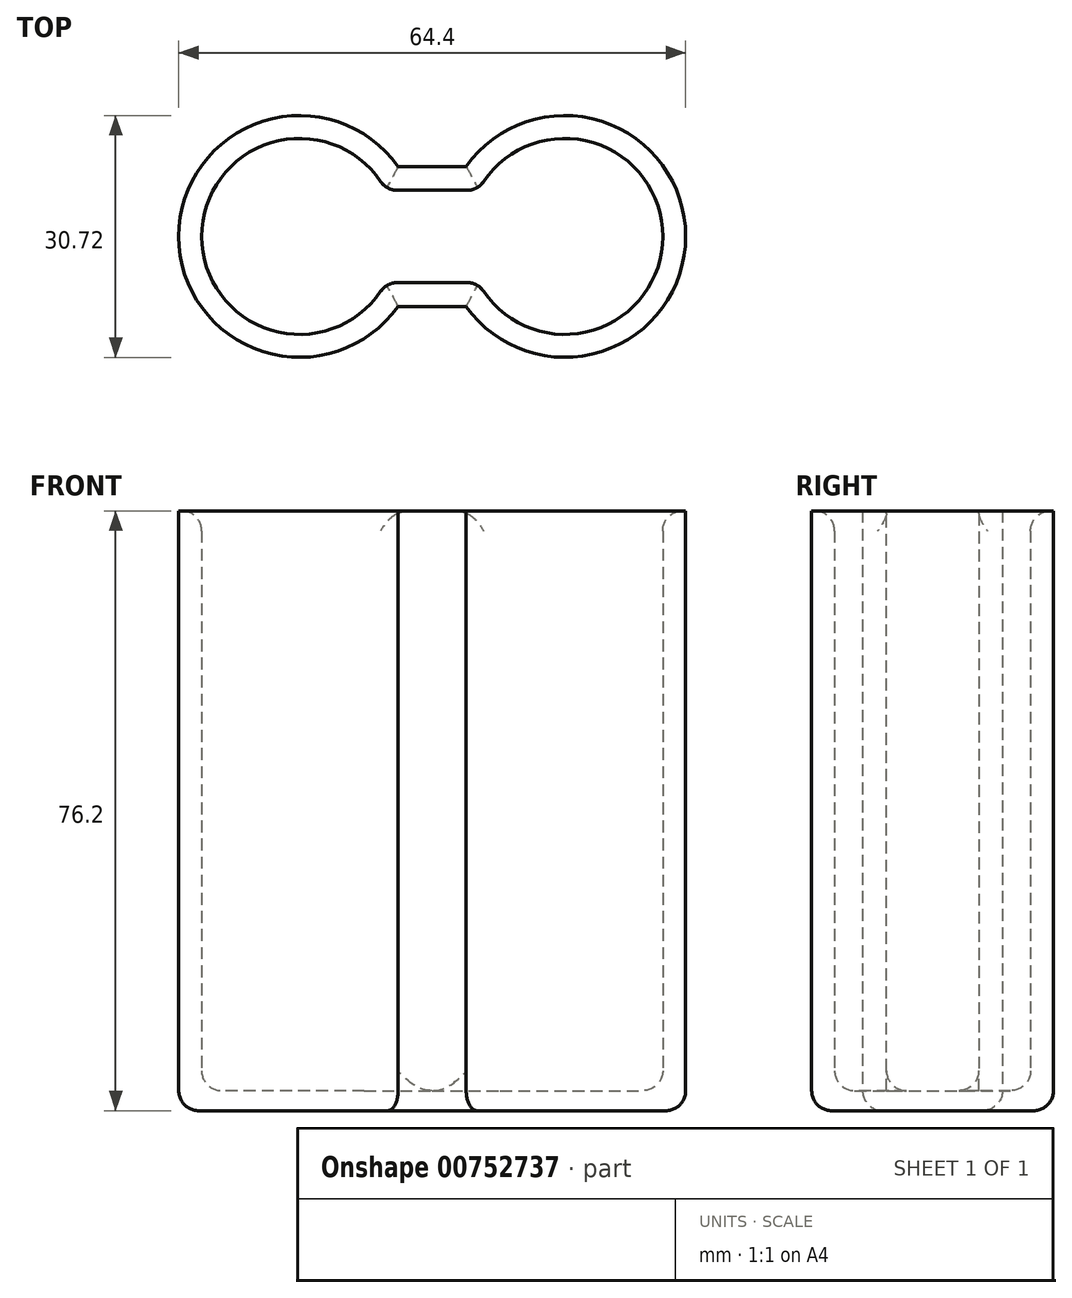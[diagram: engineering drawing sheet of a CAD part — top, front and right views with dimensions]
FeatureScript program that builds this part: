
annotation { "Feature Type Name" : "Feature", "Feature Type Description" : "" }
export const myFeature = defineFeature(function(context is Context, id is Id, definition is map)
    precondition{}
    {
        {
            var Q0;
            Q0=qCreatedBy(makeId("Top.planeOp"),FACE);
            var sketch = newSketch(context, id + "F0", { "sketchPlane" : qUnion([Q0])});
            skLineSegment(sketch, "E0.bottom", {"start": v(5.86, 5.86) * mm, "end": v(-5.86, 5.86) * mm});
            skLineSegment(sketch, "E0.top", {"start": v(5.86, -5.86) * mm, "end": v(-5.86, -5.86) * mm});
            skPoint(sketch, "E0.middle", {"position": v(0, 0) * mm});
            skArc(sketch, "E1", {"start": v(5.86, -5.86) * mm, "mid": v(29.29, 0) * mm, "end": v(5.86, 5.86) * mm});
            skArc(sketch, "E2", {"start": v(-5.86, 5.86) * mm, "mid": v(-29.29, 0) * mm, "end": v(-5.86, -5.86) * mm});
            skArc(sketch, "E3", {"start": v(-4.32, 8.9) * mm, "mid": v(-32.2, 0) * mm, "end": v(-4.32, -8.9) * mm});
            skArc(sketch, "E4", {"start": v(4.32, -8.9) * mm, "mid": v(32.2, 0) * mm, "end": v(4.32, 8.9) * mm});
            skLineSegment(sketch, "E5", {"start": v(-4.32, -8.9) * mm, "end": v(4.32, -8.9) * mm});
            skLineSegment(sketch, "E6", {"start": v(4.32, 8.9) * mm, "end": v(-4.32, 8.9) * mm});
            skSolve(sketch);
        }
        {
            var Q0;
            Q0=makeQuery(id+"F0.imprint","IMPRINT",FACE,{"disambiguationData":[TD([[makeQuery(id+"F0.imprint","IMPRINT",EDGE,{"derivedFrom":sQuery(id+"F0.wireOp",EDGE,"E0.bottom")}),1.0]])]});
            var Q1;
            Q1=makeQuery(id+"F0.imprint","IMPRINT",FACE,{"disambiguationData":[TD([[makeQuery(id+"F0.imprint","IMPRINT",EDGE,{"derivedFrom":sQuery(id+"F0.wireOp",EDGE,"E0.bottom")}),-1.0]])]});
            extrude(context, id + "F1", {"entities" : qUnion([Q0, Q1]), "depth" : 2.54 * mm, "offsetDistance" : 25.4 * mm});
        }
        {
            var Q0;
            Q0 = qSketchRegion(id + "F0", true);
            extrude(context, id + "F2", {"entities" : qUnion([Q0]), "operationType" : NewBodyOperationType.ADD, "depth" : 76.2 * mm, "offsetDistance" : 25.4 * mm});
        }
        {
            var Q0;
            Q0=makeQuery(id+"F2.opExtrude","SWEPT_FACE",FACE,{"disambiguationData":[OSD([sQuery(id+"F0.wireOp",EDGE,"E1")])]});
            fillet(context, id + "F3", {"entities" : qUnion([Q0]), "radius" : 2.54 * mm, "tangentPropagation" : true, "allowEdgeOverflow" : false});
        }
        {
            var Q0;
            Q0=makeQuery(id+"F2.opExtrude","SWEPT_FACE",FACE,{"disambiguationData":[OSD([sQuery(id+"F0.wireOp",EDGE,"E2")])]});
            fillet(context, id + "F4", {"entities" : qUnion([Q0]), "radius" : 2.54 * mm, "tangentPropagation" : true, "allowEdgeOverflow" : false});
        }
        {
            var Q0;
            Q0=makeQuery(id+"F1.opExtrude","CAP_FACE",FACE,{"disambiguationData":[OSD([sQuery(id+"F0.wireOp",EDGE,"E3"),sQuery(id+"F0.wireOp",EDGE,"E4"),sQuery(id+"F0.wireOp",EDGE,"E5"),sQuery(id+"F0.wireOp",EDGE,"E6")])],"isStart":true});
            fillet(context, id + "F5", {"entities" : qUnion([Q0]), "radius" : 2.54 * mm, "tangentPropagation" : true, "allowEdgeOverflow" : false});
        }
    });
